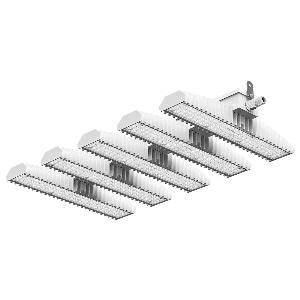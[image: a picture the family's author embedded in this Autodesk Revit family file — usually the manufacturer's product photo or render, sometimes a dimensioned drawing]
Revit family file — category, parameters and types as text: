
# Revit family: 3f_filippi_-_3f_lem_medio_3f_filippi_-_58897_-_3f_lem_5_led_250_cr_medio
name_source: partatom
category: Lighting Fixtures
units: mm (PartAtom-declared; Revit-internal decimal feet)

## family parameters
Cut with Voids When Loaded = No
Host = Face
Light Source = No
Part Type = Normal
Room Calculation Point = No
Round Connector Dimension = Use Diameter
Shared = No

## types (1)
- 3F Filippi - 3F LEM Medio (1 x LED, 41574 lm, 274 W, 4000 K)
    Apparent Load = 274 VA
    Approval mark = CE
    CIE Flux Codes = 83 96 99 100 100
    Color Rendering = 80
    Color Temperature = 4000 K
    Control Gear = Electronic ballast
    Default Elevation = 1800 mm
    Description = Industrial luminaire with high light output and high luminous efficiency designed with the most innovative technologies for environments with temperature up to 55°C.

ILLUMINOTECHNICAL
Luminous efficiency 100% (DLOR 100%, ULOR 0%).
Initial luminous flux of the luminaire 41574 lm.
Medium distribution with rectangular shape.
Installation Interdistance Transv.D = 1.02 x hu - Long.D = 1.06 x hu.
Tabular UGR (CIE 117 - 4H-8H; S=0.25H; 70/50/20): RUG 19.2 - 18.8.
Beam angle: 65° - 67°.
Luminous efficacy 152 lm/W.
Lifetime (L93/B10): 30000 h. (tq+25°C)
Lifetime (L90/B10): 50000 h. (tq+25°C)
Lifetime (L85/B10): 80000 h. (tq+25°C)
Lifetime (L80/B10): 100000 h. (tq+25°C)
Lifetime (L85/B10): 50000 h. (tq+55°C)
Sudden decreased luminous flux after 50000 hours: 0% (C0).
Photobiological safety in compliance with IEC/TR 62778: RG0 risk exempt, (IEC 62471).
In compliance with IEC/EN 62722-2-1 - IEC/EN 62717 standards.

SOURCE
5 Mid-Power linear LED modules 50W/840.
Energy efficiency class (UE 2019/2020 - UE 2019/2015): C.
CIE 13.3 Colour rendering index: CRI >80 (R9 <50%).
IES TM-30 Fidelity Index: Rf = 84 Rg = 95.
CCT nominal colour temperature 4000 K.
Colour initial tolerance (MacAdam): SDCM 3.

MECHANICAL
Passive modular heatsinks in die-casted aluminium, painted in white colour.
To optimize the thermal management of the LED module, the heatsinks are oversized and provided with self-cleaning of cooling fins.
Wiring body in aluminium and galvanised steel anchored solidly to the sinks and thermally separated.
3F Lens lenses with high luminous efficiency, transparent methacrylate (PMMA), fixed to the LED modules.
Fixing brackets in stainless steel.
Luminaire with limited surface temperature. - D - (EN 60598-2-24)
Dimensions: 952x542 mm, height 129 mm. Weight 21.645 kg.
IP65 protection degree.
Mechanical strength to impacts IK06 (1 joule).
Glow-wire test resistance 650°C.

ELECTRICAL
Halogen Free electronic wiring 230V-50/60Hz, power factor 0.97, THD <25%, constant output current, class I, 3 driver.
Power of the luminaire 274 W.
ENEC - CE.
SAFE FLICKER: PstLM=<1 and SVM=<0.4 (IEC TR 61547-1 and IEC TR 63158), to ensure a more comfortable and safe light.
Luminaire compliant with EN 60598-2-22 for power supply from a centralised emergency system CPSS (Central Power Supply System), not incorporated in the luminaire - high risk areas excluded. The default power and flux are 100% in AC and 100% in DC.
Ambient temperature from -30°C to +55°C.
Temperature class T6 max 85°C.
Quick connection via M20 3P connector with 9-13 mm tightening range.
Power unit positioned on a separate compartment by the LED module to ensure optimum temperatures of cabling components, to be inspectable and maintainable.
Relative humidity UR: <85%.

INSTALLATION
Ceiling / Suspended / Wall.
All accessories dedicated to this product are available on the Catalog and on our website www.3F-Filippi.com.

APPLICATIONS
In commercial environments, exhibition and industrial areas, stores, open areas.
Applications with high ambient temperature up to 55°C.
Environments in which it is necessary a total protection against falling fragments (eg environments with foodstuffs or machines with moving parts or with extreme temperature changes), use luminaires with polycarbonate lenses.

WARNING
Fixture not suitable for cold stores with an ambient temperature <0°C and/or relative humidity >85%.
Luminaire designed for disposal/recycling at end-of-life.
Replaceable (LED only) light source by a professional. Replaceable control gear by a professional.
    Height = 129 mm
    Lamp = 1 x LED
    Lamp Light Flux = 41574 lm
    Lamp Power = 274 W
    Lamp count = 1
    Length = 952 mm
    Lifetime = 50000 h
    Luminous efficacy = 152 lm/W
    Manufacturer = 3F Filippi
    ModVariant = No
    Model = 3F Filippi - 58897 - 3F LEM 5 LED 250 CR MEDIO
    Mounting Place = Ceiling
    Mounting Type = Pendant
    Number of Poles = 1
    OnlyDefault = Yes
    Power Factor = 1
    Product Name = 3F Filippi - 3F LEM Medio
    Product group = pendant luminaire
    ProductGroupID = 9
    Protection Class = Protection class I
    Protection Degree = IP 65
    RLX_Detail_Level = 1
    RLX_Emergency_Light_Flux = 0 lm
    RLX_Emergency_Type = 0
    RLX_Emergency_Type_DB = No
    RlxData = <blob elided: 132125 chars, md5=69672f94>
    Socket = socket
    Standby Power = 0 W
    System Light Flux = 41574 lm
    System Power = 274 W
    Type Comments = Product without accessories
    Type Image = 3f_filippi_-_lem_5.jpg
    URL = http://relux.com
    VarID = ---
    Voltage = 0 V
    Weight = 0.00 kg
    Width = 542 mm

## geometry (parser evidence)
native form markers: Blend x4, Sweep x14
no freeform markers — native parametric forms only
